# Revit family: Faucet-Wall_Mount-Lavatory-KALLISTA-Vice-P34584_1
name_source: partatom
category: Plumbing Fixtures
units: mm (PartAtom-declared; Revit-internal decimal feet)

## family parameters
Cut with Voids When Loaded = No
Host = Face
OmniClass Number = 23.31.11.00
OmniClass Title = Faucets
Part Type = Normal
Room Calculation Point = No
Round Connector Dimension = Use Diameter
Shared = No

## types (5) — shared parameters
ADA Compliant = No
Assembly Code = D2010
CW Connection = Yes
Cold Water Inlet = Cold Water Inlet
Date Modified = 05/02/2024
Default Elevation = 36"
Description = Wall Mount Sink Faucet Widespread
Drain Included = Yes
Flow Rate = 1 GPM
HW Connection = Yes
Handle Clearance = 3 1/8"
Height = 2 1/2"
Hot Water Inlet = Hot Water Inlet
Length = 8 15/16"
Manufacturer = Kohler Co.
Master Format 2014 = 22 41 39
Master Format 2014 Name = Residential Faucets, Supplies, and Trim
Material = Premium Metal Construction
Pressure = 45.00 psi
Product Name = Vice
Spout Reach = 8 15/16"
URL = https://www.kallista.com
Vent Connection = No
Waste Connection = No
Waste Water Outlet = Waste Water Outlet
WaterSense Certified = No

## per-type parameters (varying)
| type | Finish | Model | Secondary Finish | Type |
| Brushed French Gold Accent, AF-French Gold | Kallista-Plastic-BAF-Brushed_French_Gold | P34584-BAF-AF | Kallista-Metal-AF-French_Gold | 1 |
| Vibrant Brushed Nickel Accent, BGP | Kallista-Plastic-BN-Vibrant_Brushed_Nickel | P34584-BN-BGP | Kallista-Metal-BGP | 2 |
| Vibrant Brushed Nickel Accent, SN-Polished Nickel | Kallista-Plastic-BN-Vibrant_Brushed_Nickel | P34584-BN-SN | Kallista-Metal-SN-Polished_Nickel | 3 |
| Brushed Bronze Accent, CP-Chrome | Kallista-Plastic-BV-Brushed_Bronze | P34584-BV-CP | Kallista-Metal-SN-Polished_Nickel | 4 |
| Chrome Accent, CP-Chrome | Kallista-Plastic-CP-Chrome | P34584-CP-CP | Kallista-Metal-CP-Chrome | 5 |

## geometry (parser evidence)
native form markers: Sweep x7
no freeform markers — native parametric forms only
